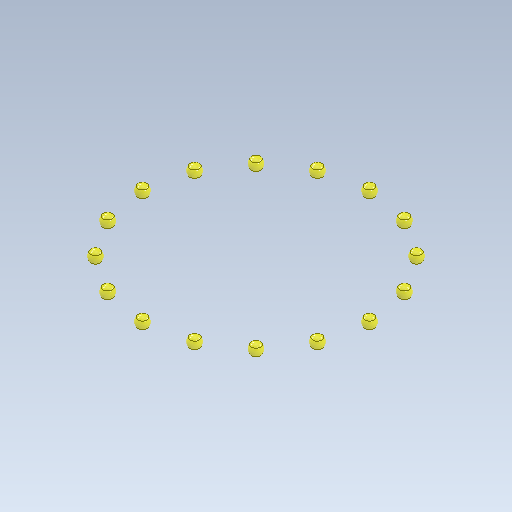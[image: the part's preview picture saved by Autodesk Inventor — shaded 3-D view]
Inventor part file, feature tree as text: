
AUTODESK INVENTOR PART (.ipt)
format: ipt  version: 2020.2 (Build 242310000, 310)  size: 264,192 bytes
history: native  units: mm
features: sketch x4, other x4, revolve x1, pattern_circular x1
ambient origin geometry x8: Origin, YZ Plane, XZ Plane, XY Plane, X Axis, Y Axis, Z Axis, Center Point
bodies: Solido1 (feature_tree), Solido2 (feature_tree), Solido3 (feature_tree), Solido4 (feature_tree), Solido5 (feature_tree)
feature tree (10):
  sketch  "Schizzo1"
  revolve  "Rivoluzione1"
  pattern_circular  "Serie circolare1"  Count=24  [1 undecoded]
  other  "Piano di lavoro2"
  other  "Divisione1"
  other  "Divisione2"
  sketch  "Schizzo2"
  other  "Punto di riferimento2"
  sketch  "Schizzo4"
  sketch  "Schizzo5"
note: 1 required parameter value undecoded (feature->parameter linkage not recoverable at this tier; creation-order binding heuristic only, values carry confidence <= 0.55)
